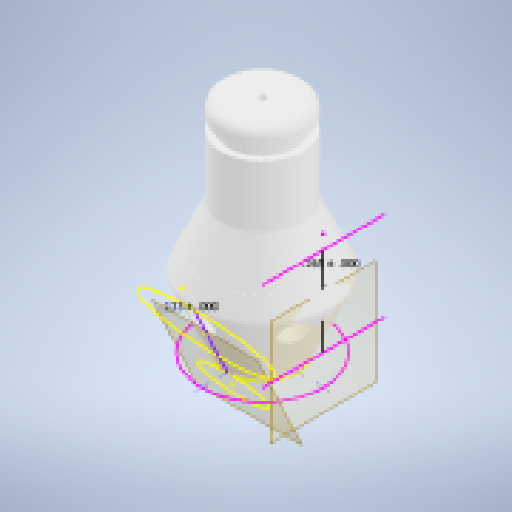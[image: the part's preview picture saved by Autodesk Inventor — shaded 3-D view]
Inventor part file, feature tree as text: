
AUTODESK INVENTOR PART (.ipt)
format: ipt  version: 2024.1 (Build 281209000, 209)  size: 322,048 bytes
history: native  units: in
note: dims shown in document units (in); Inventor stores cm internally (conversion verified against a paired STEP export)
features: hole x4, sketch x3, plane x2, fillet x2, revolve x1, pattern_circular x1
ambient origin geometry x8: Origin, YZ Plane, XZ Plane, XY Plane, X Axis, Y Axis, Z Axis, Center Point
bodies: Solid1 (feature_tree)
feature tree (13):
  revolve  "Revolution1"  [1 undecoded]
  hole  "Hole4"  [1 undecoded]
  hole  "Hole8"  [1 undecoded]
  sketch  "Sketch13"  dims[d0=0.3328in d1=0.5in]
  plane  "Work Plane6"
  sketch  "Sketch29"  dims[d2=90.0deg d3=0.057in]
  plane  "Work Plane5"
  sketch  "Sketch30"  dims[d4=0.095in d5=0.125in d6=90.0deg d23=0.65in d24=0.4466in d25=0.125in d54=0.3779in d72=0.3779in d83=0.75in d84=0.75in d85=0.0625in d86=0.75in d87=0.375in d88=0.25in d89=0.5635in d90=1.1in d91=0.8108in d92=0.2645in d121=0.196in d122=0.25in d123=0.375in d124=0.25in d125=0.5635in d126=0.25in d127=0.0in d137=0.3779in d155=0.3779in d173=0.3779in d191=0.3779in d221=0.3779in d239=0.3779in d253=0.4466in d254=0.1325in d255=0.0625in d256=0.25in d257=0.375in d258=0.25in d259=0.5635in d260=0.55in d261=0.0in d262=0.213in d263=0.25in d264=0.375in d265=0.25in d266=0.5635in d267=0.25in d268=0.0in d269=1.5748in d270=1.3743in d272=0.0625in d273=0.0625in]
  hole  "Hole9"  [1 undecoded]
  hole  "Hole10"  [1 undecoded]
  pattern_circular  "Circular Pattern7"  [2 undecoded]
  fillet  "Fillet1"  Radius=0.125in
  fillet  "Fillet2"  Radius=0.3779in
note: 7 required parameter values undecoded (feature->parameter linkage not recoverable at this tier; creation-order binding heuristic only, values carry confidence <= 0.55)